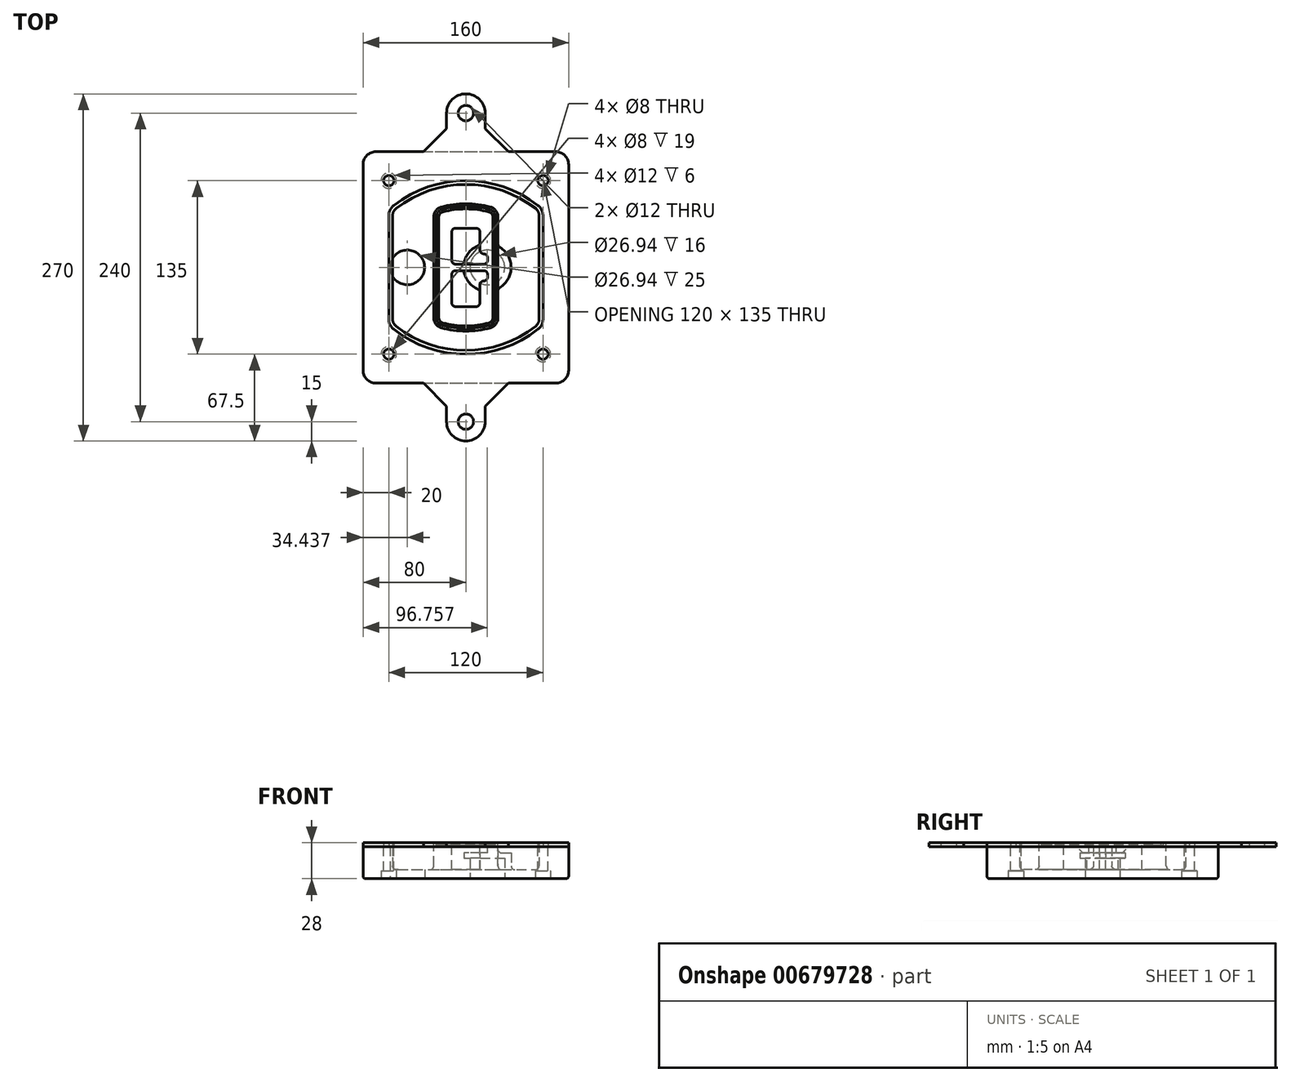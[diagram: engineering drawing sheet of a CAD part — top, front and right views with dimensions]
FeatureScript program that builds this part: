
annotation { "Feature Type Name" : "Feature", "Feature Type Description" : "" }
export const myFeature = defineFeature(function(context is Context, id is Id, definition is map)
    precondition{}
    {
        {
            var Q0;
            Q0=qCreatedBy(makeId("Top.planeOp"),FACE);
            var sketch = newSketch(context, id + "F0", { "sketchPlane" : qUnion([Q0])});
            skPoint(sketch, "E0.rect.middle", {"position": v(0, 0) * mm});
            skLineSegment(sketch, "E1.bottom", {"start": v(-70, -90) * mm, "end": v(70, -90) * mm});
            skLineSegment(sketch, "E1.top", {"start": v(-70, 90) * mm, "end": v(70, 90) * mm});
            skLineSegment(sketch, "E1.left", {"start": v(-80, -80) * mm, "end": v(-80, 80) * mm});
            skLineSegment(sketch, "E1.right", {"start": v(80, -80) * mm, "end": v(80, 80) * mm});
            skLineSegment(sketch, "E2", {"start": v(-80, 90) * mm, "end": v(80, -90) * mm, "construction": true});
            skLineSegment(sketch, "E3", {"start": v(80, 90) * mm, "end": v(-80, -90) * mm, "construction": true});
            skCircle(sketch, "E4", {"center": v(-60, 67.5) * mm, "radius": 4 * mm});
            skCircle(sketch, "E5", {"center": v(60, 67.5) * mm, "radius": 4 * mm});
            skCircle(sketch, "E6", {"center": v(60, -67.5) * mm, "radius": 4 * mm});
            skCircle(sketch, "E7", {"center": v(-60, -67.5) * mm, "radius": 4 * mm});
            skLineSegment(sketch, "E8", {"start": v(-60, 67.5) * mm, "end": v(60, 67.5) * mm, "construction": true});
            skLineSegment(sketch, "E9", {"start": v(60, 67.5) * mm, "end": v(60, -67.5) * mm, "construction": true});
            skLineSegment(sketch, "E10", {"start": v(60, -67.5) * mm, "end": v(-60, -67.5) * mm, "construction": true});
            skLineSegment(sketch, "E11", {"start": v(-60, -67.5) * mm, "end": v(-60, 67.5) * mm, "construction": true});
            skLineSegment(sketch, "E12", {"start": v(-60, 40.3) * mm, "end": v(-60, -40.3) * mm});
            skLineSegment(sketch, "E13", {"start": v(60, 40.3) * mm, "end": v(60, -40.3) * mm});
            skArc(sketch, "E14", {"start": v(56.15, 48.18) * mm, "mid": v(0, 67.5) * mm, "end": v(-56.15, 48.18) * mm});
            skArc(sketch, "E15", {"start": v(-56.15, -48.18) * mm, "mid": v(0, -67.5) * mm, "end": v(56.15, -48.18) * mm});
            skLineSegment(sketch, "E16", {"start": v(-60, 0) * mm, "end": v(60, 0) * mm, "construction": true});
            skPoint(sketch, "E17.visualSharp", {"position": v(-60, -45) * mm});
            skArc(sketch, "E17.filletArc", {"start": v(-60, -40.3) * mm, "mid": v(-58.99, -44.68) * mm, "end": v(-56.15, -48.18) * mm});
            skPoint(sketch, "E18.visualSharp", {"position": v(-60, 45) * mm});
            skArc(sketch, "E18.filletArc", {"start": v(-56.15, 48.18) * mm, "mid": v(-58.99, 44.68) * mm, "end": v(-60, 40.3) * mm});
            skPoint(sketch, "E19.visualSharp", {"position": v(60, 45) * mm});
            skArc(sketch, "E19.filletArc", {"start": v(60, 40.3) * mm, "mid": v(58.99, 44.68) * mm, "end": v(56.15, 48.18) * mm});
            skPoint(sketch, "E20.visualSharp", {"position": v(60, -45) * mm});
            skArc(sketch, "E20.filletArc", {"start": v(56.15, -48.18) * mm, "mid": v(58.99, -44.68) * mm, "end": v(60, -40.3) * mm});
            skPoint(sketch, "E21.visualSharp", {"position": v(-80, 90) * mm});
            skArc(sketch, "E21.filletArc", {"start": v(-70, 90) * mm, "mid": v(-77.07, 87.07) * mm, "end": v(-80, 80) * mm});
            skPoint(sketch, "E22.visualSharp", {"position": v(80, 90) * mm});
            skArc(sketch, "E22.filletArc", {"start": v(80, 80) * mm, "mid": v(77.07, 87.07) * mm, "end": v(70, 90) * mm});
            skPoint(sketch, "E23.visualSharp", {"position": v(80, -90) * mm});
            skArc(sketch, "E23.filletArc", {"start": v(70, -90) * mm, "mid": v(77.07, -87.07) * mm, "end": v(80, -80) * mm});
            skPoint(sketch, "E24.visualSharp", {"position": v(-80, -90) * mm});
            skArc(sketch, "E24.filletArc", {"start": v(-80, -80) * mm, "mid": v(-77.07, -87.07) * mm, "end": v(-70, -90) * mm});
            skArc(sketch, "E25.0", {"start": v(57, 40.3) * mm, "mid": v(56.3, 43.36) * mm, "end": v(54.3, 45.81) * mm});
            skLineSegment(sketch, "E25.1", {"start": v(57, 40.3) * mm, "end": v(57, -40.3) * mm});
            skArc(sketch, "E25.2", {"start": v(54.3, -45.81) * mm, "mid": v(56.3, -43.36) * mm, "end": v(57, -40.3) * mm});
            skArc(sketch, "E25.3", {"start": v(-54.3, -45.81) * mm, "mid": v(0, -64.5) * mm, "end": v(54.3, -45.81) * mm});
            skArc(sketch, "E25.4", {"start": v(-57, -40.3) * mm, "mid": v(-56.3, -43.36) * mm, "end": v(-54.3, -45.81) * mm});
            skArc(sketch, "E25.5", {"start": v(54.3, 45.81) * mm, "mid": v(0, 64.5) * mm, "end": v(-54.3, 45.81) * mm});
            skLineSegment(sketch, "E25.6", {"start": v(-57, 40.3) * mm, "end": v(-57, -40.3) * mm});
            skArc(sketch, "E25.7", {"start": v(-54.3, 45.81) * mm, "mid": v(-56.3, 43.36) * mm, "end": v(-57, 40.3) * mm});
            skArc(sketch, "E26.0", {"start": v(-58.62, 51.33) * mm, "mid": v(-62.58, 46.43) * mm, "end": v(-64, 40.3) * mm});
            skArc(sketch, "E26.1", {"start": v(58.62, 51.33) * mm, "mid": v(0, 71.5) * mm, "end": v(-58.62, 51.33) * mm});
            skArc(sketch, "E26.2", {"start": v(64, 40.3) * mm, "mid": v(62.58, 46.43) * mm, "end": v(58.62, 51.33) * mm});
            skLineSegment(sketch, "E26.3", {"start": v(64, 40.3) * mm, "end": v(64, -40.3) * mm});
            skArc(sketch, "E26.4", {"start": v(58.62, -51.33) * mm, "mid": v(62.58, -46.43) * mm, "end": v(64, -40.3) * mm});
            skLineSegment(sketch, "E26.5", {"start": v(-64, 40.3) * mm, "end": v(-64, -40.3) * mm});
            skArc(sketch, "E26.6", {"start": v(-58.62, -51.33) * mm, "mid": v(0, -71.5) * mm, "end": v(58.62, -51.33) * mm});
            skArc(sketch, "E26.7", {"start": v(-64, -40.3) * mm, "mid": v(-62.58, -46.43) * mm, "end": v(-58.62, -51.33) * mm});
            skSolve(sketch);
        }
        {
            var Q0;
            Q0=makeQuery(id+"F0.imprint","IMPRINT",FACE,{"disambiguationData":[TD([[makeQuery(id+"F0.imprint","IMPRINT",EDGE,{"derivedFrom":sQuery(id+"F0.wireOp",EDGE,"E1.bottom")}),1.0]])]});
            var Q1;
            Q1=makeQuery(id+"F0.imprint","IMPRINT",FACE,{"disambiguationData":[TD([[makeQuery(id+"F0.imprint","IMPRINT",EDGE,{"derivedFrom":sQuery(id+"F0.wireOp",EDGE,"E12")}),1.0]])]});
            var Q2;
            Q2=makeQuery(id+"F0.imprint","IMPRINT",FACE,{"disambiguationData":[TD([[makeQuery(id+"F0.imprint","IMPRINT",EDGE,{"derivedFrom":sQuery(id+"F0.wireOp",EDGE,"E25.0")}),1.0]])]});
            var Q3;
            Q3=makeQuery(id+"F0.imprint","IMPRINT",FACE,{"disambiguationData":[TD([[makeQuery(id+"F0.imprint","IMPRINT",EDGE,{"derivedFrom":sQuery(id+"F0.wireOp",EDGE,"E12")}),-1.0]])]});
            extrude(context, id + "F1", {"entities" : qUnion([Q0, Q1, Q2, Q3]), "oppositeDirection" : true, "depth" : 25 * mm});
        }
        {
            var Q0;
            Q0=makeQuery(id+"F0.imprint","IMPRINT",FACE,{"disambiguationData":[TD([[makeQuery(id+"F0.imprint","IMPRINT",EDGE,{"derivedFrom":sQuery(id+"F0.wireOp",EDGE,"E12")}),1.0]])]});
            extrude(context, id + "F2", {"entities" : qUnion([Q0]), "operationType" : NewBodyOperationType.ADD, "depth" : 3 * mm});
        }
        {
            var Q0;
            Q0=makeQuery(id+"F0.imprint","IMPRINT",FACE,{"disambiguationData":[TD([[makeQuery(id+"F0.imprint","IMPRINT",EDGE,{"derivedFrom":sQuery(id+"F0.wireOp",EDGE,"E25.0")}),1.0]])]});
            extrude(context, id + "F3", {"entities" : qUnion([Q0]), "operationType" : NewBodyOperationType.REMOVE, "oppositeDirection" : true, "depth" : 18 * mm});
        }
        {
            var Q0;
            Q0=makeQuery(id+"F2.opExtrude","CAP_FACE",FACE,{"disambiguationData":[OSD([sQuery(id+"F0.wireOp",EDGE,"E12"),sQuery(id+"F0.wireOp",EDGE,"E13"),sQuery(id+"F0.wireOp",EDGE,"E14"),sQuery(id+"F0.wireOp",EDGE,"E15"),sQuery(id+"F0.wireOp",EDGE,"E17.filletArc"),sQuery(id+"F0.wireOp",EDGE,"E18.filletArc"),sQuery(id+"F0.wireOp",EDGE,"E19.filletArc"),sQuery(id+"F0.wireOp",EDGE,"E20.filletArc"),sQuery(id+"F0.wireOp",EDGE,"E25.0"),sQuery(id+"F0.wireOp",EDGE,"E25.1"),sQuery(id+"F0.wireOp",EDGE,"E25.2"),sQuery(id+"F0.wireOp",EDGE,"E25.3"),sQuery(id+"F0.wireOp",EDGE,"E25.4"),sQuery(id+"F0.wireOp",EDGE,"E25.5"),sQuery(id+"F0.wireOp",EDGE,"E25.6"),sQuery(id+"F0.wireOp",EDGE,"E25.7")])],"isStart":false});
            var sketch = newSketch(context, id + "F4", { "sketchPlane" : qUnion([Q0])});
            skArc(sketch, "E27.0", {"start": v(-19.08, -46.97) * mm, "mid": v(0, -49.5) * mm, "end": v(19.08, -46.97) * mm});
            skArc(sketch, "E28.0", {"start": v(19.08, 46.97) * mm, "mid": v(0, 49.5) * mm, "end": v(-19.08, 46.97) * mm});
            skLineSegment(sketch, "E29", {"start": v(-25, 39.25) * mm, "end": v(-25, -39.25) * mm});
            skLineSegment(sketch, "E30", {"start": v(25, 39.25) * mm, "end": v(25, -39.25) * mm});
            skLineSegment(sketch, "E31", {"start": v(-25, 45.1) * mm, "end": v(25, 45.1) * mm, "construction": true});
            skLineSegment(sketch, "E32", {"start": v(-25, -45.1) * mm, "end": v(25, -45.1) * mm, "construction": true});
            skPoint(sketch, "E33.visualSharp", {"position": v(-25, 45.1) * mm});
            skArc(sketch, "E33.filletArc", {"start": v(-19.08, 46.97) * mm, "mid": v(-23.35, 44.11) * mm, "end": v(-25, 39.25) * mm});
            skPoint(sketch, "E34.visualSharp", {"position": v(25, 45.1) * mm});
            skArc(sketch, "E34.filletArc", {"start": v(25, 39.25) * mm, "mid": v(23.35, 44.11) * mm, "end": v(19.08, 46.97) * mm});
            skPoint(sketch, "E35.visualSharp", {"position": v(25, -45.1) * mm});
            skArc(sketch, "E35.filletArc", {"start": v(19.08, -46.97) * mm, "mid": v(23.35, -44.11) * mm, "end": v(25, -39.25) * mm});
            skPoint(sketch, "E36.visualSharp", {"position": v(-25, -45.1) * mm});
            skArc(sketch, "E36.filletArc", {"start": v(-25, -39.25) * mm, "mid": v(-23.35, -44.11) * mm, "end": v(-19.08, -46.97) * mm});
            skArc(sketch, "E37.0", {"start": v(54.3, 45.81) * mm, "mid": v(0, 64.5) * mm, "end": v(-54.3, 45.81) * mm});
            skArc(sketch, "E37.1", {"start": v(-54.3, 45.81) * mm, "mid": v(-56.3, 43.36) * mm, "end": v(-57, 40.3) * mm});
            skLineSegment(sketch, "E37.2", {"start": v(-57, 40.3) * mm, "end": v(-57, -40.3) * mm});
            skArc(sketch, "E37.3", {"start": v(-57, -40.3) * mm, "mid": v(-56.3, -43.36) * mm, "end": v(-54.3, -45.81) * mm});
            skArc(sketch, "E37.4", {"start": v(-54.3, -45.81) * mm, "mid": v(0, -64.5) * mm, "end": v(54.3, -45.81) * mm});
            skArc(sketch, "E37.5", {"start": v(54.3, -45.81) * mm, "mid": v(56.3, -43.36) * mm, "end": v(57, -40.3) * mm});
            skLineSegment(sketch, "E37.6", {"start": v(57, 40.3) * mm, "end": v(57, -40.3) * mm});
            skArc(sketch, "E37.7", {"start": v(57, 40.3) * mm, "mid": v(56.3, 43.36) * mm, "end": v(54.3, 45.81) * mm});
            skLineSegment(sketch, "E38.0", {"start": v(23, 39.25) * mm, "end": v(23, -39.25) * mm});
            skArc(sketch, "E38.1", {"start": v(18.56, -45.04) * mm, "mid": v(21.76, -42.9) * mm, "end": v(23, -39.25) * mm});
            skArc(sketch, "E38.2", {"start": v(-18.56, -45.04) * mm, "mid": v(0, -47.5) * mm, "end": v(18.56, -45.04) * mm});
            skArc(sketch, "E38.3", {"start": v(-23, -39.25) * mm, "mid": v(-21.76, -42.9) * mm, "end": v(-18.56, -45.04) * mm});
            skLineSegment(sketch, "E38.4", {"start": v(-23, 39.25) * mm, "end": v(-23, -39.25) * mm});
            skArc(sketch, "E38.5", {"start": v(23, 39.25) * mm, "mid": v(21.76, 42.9) * mm, "end": v(18.56, 45.04) * mm});
            skArc(sketch, "E38.6", {"start": v(-18.56, 45.04) * mm, "mid": v(-21.76, 42.9) * mm, "end": v(-23, 39.25) * mm});
            skArc(sketch, "E38.7", {"start": v(18.56, 45.04) * mm, "mid": v(0, 47.5) * mm, "end": v(-18.56, 45.04) * mm});
            skArc(sketch, "E39.0", {"start": v(21, 39.25) * mm, "mid": v(20.18, 41.68) * mm, "end": v(18.04, 43.1) * mm});
            skLineSegment(sketch, "E39.1", {"start": v(21, 39.25) * mm, "end": v(21, -39.25) * mm});
            skArc(sketch, "E39.2", {"start": v(18.04, -43.1) * mm, "mid": v(20.18, -41.68) * mm, "end": v(21, -39.25) * mm});
            skArc(sketch, "E39.3", {"start": v(-18.04, -43.1) * mm, "mid": v(0, -45.5) * mm, "end": v(18.04, -43.1) * mm});
            skArc(sketch, "E39.4", {"start": v(-21, -39.25) * mm, "mid": v(-20.18, -41.68) * mm, "end": v(-18.04, -43.1) * mm});
            skArc(sketch, "E39.5", {"start": v(18.04, 43.1) * mm, "mid": v(0, 45.5) * mm, "end": v(-18.04, 43.1) * mm});
            skLineSegment(sketch, "E39.6", {"start": v(-21, 39.25) * mm, "end": v(-21, -39.25) * mm});
            skArc(sketch, "E39.7", {"start": v(-18.04, 43.1) * mm, "mid": v(-20.18, 41.68) * mm, "end": v(-21, 39.25) * mm});
            skLineSegment(sketch, "E40", {"start": v(-25, 0) * mm, "end": v(25, 0) * mm, "construction": true});
            skLineSegment(sketch, "E41", {"start": v(-11, 5.5) * mm, "end": v(-11, 27.5) * mm});
            skLineSegment(sketch, "E42", {"start": v(-8, 30.5) * mm, "end": v(8, 30.5) * mm});
            skLineSegment(sketch, "E43", {"start": v(11, 27.5) * mm, "end": v(11, 13.5) * mm});
            skLineSegment(sketch, "E44", {"start": v(14, 10.5) * mm, "end": v(14, 10.5) * mm});
            skLineSegment(sketch, "E45", {"start": v(17, 7.5) * mm, "end": v(17, 5.5) * mm});
            skLineSegment(sketch, "E46", {"start": v(14, 2.5) * mm, "end": v(-8, 2.5) * mm});
            skPoint(sketch, "E47.visualSharp", {"position": v(-11, 30.5) * mm});
            skArc(sketch, "E47.filletArc", {"start": v(-8, 30.5) * mm, "mid": v(-10.12, 29.62) * mm, "end": v(-11, 27.5) * mm});
            skPoint(sketch, "E48.visualSharp", {"position": v(11, 30.5) * mm});
            skArc(sketch, "E48.filletArc", {"start": v(11, 27.5) * mm, "mid": v(10.12, 29.62) * mm, "end": v(8, 30.5) * mm});
            skPoint(sketch, "E49.visualSharp", {"position": v(11, 10.5) * mm});
            skArc(sketch, "E49.filletArc", {"start": v(11, 13.5) * mm, "mid": v(11.88, 11.38) * mm, "end": v(14, 10.5) * mm});
            skPoint(sketch, "E50.visualSharp", {"position": v(17, 10.5) * mm});
            skArc(sketch, "E50.filletArc", {"start": v(17, 7.5) * mm, "mid": v(16.12, 9.62) * mm, "end": v(14, 10.5) * mm});
            skPoint(sketch, "E51.visualSharp", {"position": v(17, 2.5) * mm});
            skArc(sketch, "E51.filletArc", {"start": v(14, 2.5) * mm, "mid": v(16.12, 3.38) * mm, "end": v(17, 5.5) * mm});
            skPoint(sketch, "E52.visualSharp", {"position": v(-11, 2.5) * mm});
            skArc(sketch, "E52.filletArc", {"start": v(-11, 5.5) * mm, "mid": v(-10.12, 3.38) * mm, "end": v(-8, 2.5) * mm});
            skLineSegment(sketch, "E53.0.MirrorCS", {"start": v(14, -2.5) * mm, "end": v(-8, -2.5) * mm});
            skArc(sketch, "E54.0.MirrorCS", {"start": v(-11, -5.5) * mm, "mid": v(-10.12, -3.38) * mm, "end": v(-8, -2.5) * mm});
            skLineSegment(sketch, "E55.0.MirrorCS", {"start": v(-11, -5.5) * mm, "end": v(-11, -27.5) * mm});
            skArc(sketch, "E56.0.MirrorCS", {"start": v(-8, -30.5) * mm, "mid": v(-10.12, -29.62) * mm, "end": v(-11, -27.5) * mm});
            skLineSegment(sketch, "E57.0.MirrorCS", {"start": v(-8, -30.5) * mm, "end": v(8, -30.5) * mm});
            skArc(sketch, "E58.0.MirrorCS", {"start": v(11, -27.5) * mm, "mid": v(10.12, -29.62) * mm, "end": v(8, -30.5) * mm});
            skLineSegment(sketch, "E59.0.MirrorCS", {"start": v(11, -27.5) * mm, "end": v(11, -13.5) * mm});
            skArc(sketch, "E60.0.MirrorCS", {"start": v(11, -13.5) * mm, "mid": v(11.88, -11.38) * mm, "end": v(14, -10.5) * mm});
            skArc(sketch, "E61.0.MirrorCS", {"start": v(17, -7.5) * mm, "mid": v(16.12, -9.62) * mm, "end": v(14, -10.5) * mm});
            skLineSegment(sketch, "E62.0.MirrorCS", {"start": v(17, -7.5) * mm, "end": v(17, -5.5) * mm});
            skArc(sketch, "E63.0.MirrorCS", {"start": v(14, -2.5) * mm, "mid": v(16.12, -3.38) * mm, "end": v(17, -5.5) * mm});
            skSolve(sketch);
        }
        {
            var Q0;
            Q0=makeQuery(id+"F4.imprint","IMPRINT",FACE,{"disambiguationData":[TD([[makeQuery(id+"F4.imprint","IMPRINT",EDGE,{"derivedFrom":sQuery(id+"F4.wireOp",EDGE,"E27.0")}),1.0]])]});
            var Q1;
            Q1=makeQuery(id+"F4.imprint","IMPRINT",FACE,{"disambiguationData":[TD([[makeQuery(id+"F4.imprint","IMPRINT",EDGE,{"derivedFrom":sQuery(id+"F4.wireOp",EDGE,"E38.0")}),-1.0]])]});
            var Q2;
            Q2=makeQuery(id+"F4.imprint","IMPRINT",FACE,{"disambiguationData":[TD([[makeQuery(id+"F4.imprint","IMPRINT",EDGE,{"derivedFrom":sQuery(id+"F4.wireOp",EDGE,"E39.0")}),1.0]])]});
            extrude(context, id + "F5", {"entities" : qUnion([Q0, Q1, Q2]), "operationType" : NewBodyOperationType.ADD, "endBound" : BoundingType.UP_TO_NEXT, "oppositeDirection" : true, "depth" : 25 * mm});
        }
        {
            var Q0;
            Q0=makeQuery(id+"F4.imprint","IMPRINT",FACE,{"disambiguationData":[TD([[makeQuery(id+"F4.imprint","IMPRINT",EDGE,{"derivedFrom":sQuery(id+"F4.wireOp",EDGE,"E38.0")}),-1.0]])]});
            extrude(context, id + "F6", {"entities" : qUnion([Q0]), "operationType" : NewBodyOperationType.REMOVE, "oppositeDirection" : true, "depth" : 2 * mm});
        }
        {
            var Q0;
            Q0=makeQuery(id+"F1.opExtrude","CAP_FACE",FACE,{"disambiguationData":[OSD([sQuery(id+"F0.wireOp",EDGE,"E1.bottom"),sQuery(id+"F0.wireOp",EDGE,"E1.top"),sQuery(id+"F0.wireOp",EDGE,"E1.left"),sQuery(id+"F0.wireOp",EDGE,"E1.right"),sQuery(id+"F0.wireOp",EDGE,"E4"),sQuery(id+"F0.wireOp",EDGE,"E5"),sQuery(id+"F0.wireOp",EDGE,"E6"),sQuery(id+"F0.wireOp",EDGE,"E7"),sQuery(id+"F0.wireOp",EDGE,"E21.filletArc"),sQuery(id+"F0.wireOp",EDGE,"E22.filletArc"),sQuery(id+"F0.wireOp",EDGE,"E23.filletArc"),sQuery(id+"F0.wireOp",EDGE,"E24.filletArc")])],"isStart":false});
            var sketch = newSketch(context, id + "F7", { "sketchPlane" : qUnion([Q0])});
            skCircle(sketch, "E64", {"center": v(16.76, 0) * mm, "radius": 13.47 * mm});
            skCircle(sketch, "E65", {"center": v(-45.56, 0) * mm, "radius": 13.47 * mm});
            skLineSegment(sketch, "E66", {"start": v(80, 0) * mm, "end": v(-80, 0) * mm});
            skCircle(sketch, "E67", {"center": v(16.76, 0) * mm, "radius": 18.47 * mm});
            skCircle(sketch, "E68", {"center": v(60, -67.5) * mm, "radius": 6 * mm});
            skCircle(sketch, "E69", {"center": v(-60, -67.5) * mm, "radius": 6 * mm});
            skCircle(sketch, "E70", {"center": v(-60, 67.5) * mm, "radius": 6 * mm});
            skCircle(sketch, "E71", {"center": v(60, 67.5) * mm, "radius": 6 * mm});
            skSolve(sketch);
        }
        {
            var Q0;
            {var subQ1=sQuery(id+"F7.wireOp",EDGE,"E66");var subQ4=sQuery(id+"F7.wireOp",EDGE,"E64");var subQ6=makeQuery(id+"F7.imprint","INTERSECT",VERTEX,{"disambiguationData":[OD(0.0)],"derivedFrom":[subQ4,subQ1]});Q0=makeQuery(id+"F7.imprint","IMPRINT",FACE,{"disambiguationData":[TD([[makeQuery(id+"F7.imprint","IMPRINT",EDGE,{"disambiguationData":[TD([[subQ6,-1.0]])],"derivedFrom":subQ4}),-1.0]])]});}
            var Q1;
            {var subQ0=sQuery(id+"F7.wireOp",EDGE,"E66");var subQ1=sQuery(id+"F7.wireOp",EDGE,"E64");var subQ3=makeQuery(id+"F7.imprint","INTERSECT",VERTEX,{"disambiguationData":[OD(0.0)],"derivedFrom":[subQ1,subQ0]});Q1=makeQuery(id+"F7.imprint","IMPRINT",FACE,{"disambiguationData":[TD([[makeQuery(id+"F7.imprint","IMPRINT",EDGE,{"disambiguationData":[TD([[subQ3,-1.0]])],"derivedFrom":subQ1}),1.0]])]});}
            var Q2;
            {var subQ0=sQuery(id+"F7.wireOp",EDGE,"E66");var subQ1=sQuery(id+"F7.wireOp",EDGE,"E64");var subQ3=makeQuery(id+"F7.imprint","INTERSECT",VERTEX,{"disambiguationData":[OD(0.0)],"derivedFrom":[subQ1,subQ0]});Q2=makeQuery(id+"F7.imprint","IMPRINT",FACE,{"disambiguationData":[TD([[makeQuery(id+"F7.imprint","IMPRINT",EDGE,{"disambiguationData":[TD([[subQ3,1.0]])],"derivedFrom":subQ1}),1.0]])]});}
            var Q3;
            {var subQ1=sQuery(id+"F7.wireOp",EDGE,"E66");var subQ4=sQuery(id+"F7.wireOp",EDGE,"E64");var subQ6=makeQuery(id+"F7.imprint","INTERSECT",VERTEX,{"disambiguationData":[OD(0.0)],"derivedFrom":[subQ4,subQ1]});Q3=makeQuery(id+"F7.imprint","IMPRINT",FACE,{"disambiguationData":[TD([[makeQuery(id+"F7.imprint","IMPRINT",EDGE,{"disambiguationData":[TD([[subQ6,1.0]])],"derivedFrom":subQ4}),-1.0]])]});}
            extrude(context, id + "F8", {"entities" : qUnion([Q0, Q1, Q2, Q3]), "operationType" : NewBodyOperationType.ADD, "oppositeDirection" : true, "depth" : 20 * mm});
        }
        {
            var Q0;
            {var subQ0=sQuery(id+"F7.wireOp",EDGE,"E66");var subQ1=sQuery(id+"F7.wireOp",EDGE,"E64");var subQ3=makeQuery(id+"F7.imprint","INTERSECT",VERTEX,{"disambiguationData":[OD(0.0)],"derivedFrom":[subQ1,subQ0]});Q0=makeQuery(id+"F7.imprint","IMPRINT",FACE,{"disambiguationData":[TD([[makeQuery(id+"F7.imprint","IMPRINT",EDGE,{"disambiguationData":[TD([[subQ3,-1.0]])],"derivedFrom":subQ1}),1.0]])]});}
            var Q1;
            {var subQ0=sQuery(id+"F7.wireOp",EDGE,"E66");var subQ1=sQuery(id+"F7.wireOp",EDGE,"E64");var subQ3=makeQuery(id+"F7.imprint","INTERSECT",VERTEX,{"disambiguationData":[OD(0.0)],"derivedFrom":[subQ1,subQ0]});Q1=makeQuery(id+"F7.imprint","IMPRINT",FACE,{"disambiguationData":[TD([[makeQuery(id+"F7.imprint","IMPRINT",EDGE,{"disambiguationData":[TD([[subQ3,1.0]])],"derivedFrom":subQ1}),1.0]])]});}
            extrude(context, id + "F9", {"entities" : qUnion([Q0, Q1]), "operationType" : NewBodyOperationType.REMOVE, "oppositeDirection" : true, "depth" : 16 * mm});
        }
        {
            var Q0;
            {var subQ0=sQuery(id+"F7.wireOp",EDGE,"E66");var subQ1=sQuery(id+"F7.wireOp",EDGE,"E65");var subQ3=makeQuery(id+"F7.imprint","INTERSECT",VERTEX,{"disambiguationData":[OD(0.0)],"derivedFrom":[subQ1,subQ0]});Q0=makeQuery(id+"F7.imprint","IMPRINT",FACE,{"disambiguationData":[TD([[makeQuery(id+"F7.imprint","IMPRINT",EDGE,{"disambiguationData":[TD([[subQ3,-1.0]])],"derivedFrom":subQ1}),1.0]])]});}
            var Q1;
            {var subQ0=sQuery(id+"F7.wireOp",EDGE,"E66");var subQ1=sQuery(id+"F7.wireOp",EDGE,"E65");var subQ3=makeQuery(id+"F7.imprint","INTERSECT",VERTEX,{"disambiguationData":[OD(0.0)],"derivedFrom":[subQ1,subQ0]});Q1=makeQuery(id+"F7.imprint","IMPRINT",FACE,{"disambiguationData":[TD([[makeQuery(id+"F7.imprint","IMPRINT",EDGE,{"disambiguationData":[TD([[subQ3,1.0]])],"derivedFrom":subQ1}),1.0]])]});}
            extrude(context, id + "F10", {"entities" : qUnion([Q0, Q1]), "operationType" : NewBodyOperationType.REMOVE, "oppositeDirection" : true, "depth" : 25 * mm});
        }
        {
            var Q0;
            Q0=makeQuery(id+"F7.imprint","IMPRINT",FACE,{"disambiguationData":[TD([[makeQuery(id+"F7.imprint","IMPRINT",EDGE,{"derivedFrom":sQuery(id+"F7.wireOp",EDGE,"E68")}),1.0]])]});
            var Q1;
            Q1=makeQuery(id+"F7.imprint","IMPRINT",FACE,{"disambiguationData":[TD([[makeQuery(id+"F7.imprint","IMPRINT",EDGE,{"derivedFrom":makeQuery(id+"F1.opExtrude","CAP_EDGE",EDGE,{"disambiguationData":[OSD([sQuery(id+"F0.wireOp",EDGE,"E5")])],"isStart":false})}),-1.0]])]});
            var Q2;
            Q2=makeQuery(id+"F7.imprint","IMPRINT",FACE,{"disambiguationData":[TD([[makeQuery(id+"F7.imprint","IMPRINT",EDGE,{"derivedFrom":sQuery(id+"F7.wireOp",EDGE,"E69")}),1.0]])]});
            var Q3;
            Q3=makeQuery(id+"F7.imprint","IMPRINT",FACE,{"disambiguationData":[TD([[makeQuery(id+"F7.imprint","IMPRINT",EDGE,{"derivedFrom":makeQuery(id+"F1.opExtrude","CAP_EDGE",EDGE,{"disambiguationData":[OSD([sQuery(id+"F0.wireOp",EDGE,"E4")])],"isStart":false})}),-1.0]])]});
            var Q4;
            Q4=makeQuery(id+"F7.imprint","IMPRINT",FACE,{"disambiguationData":[TD([[makeQuery(id+"F7.imprint","IMPRINT",EDGE,{"derivedFrom":sQuery(id+"F7.wireOp",EDGE,"E70")}),1.0]])]});
            var Q5;
            Q5=makeQuery(id+"F7.imprint","IMPRINT",FACE,{"disambiguationData":[TD([[makeQuery(id+"F7.imprint","IMPRINT",EDGE,{"derivedFrom":makeQuery(id+"F1.opExtrude","CAP_EDGE",EDGE,{"disambiguationData":[OSD([sQuery(id+"F0.wireOp",EDGE,"E7")])],"isStart":false})}),-1.0]])]});
            var Q6;
            Q6=makeQuery(id+"F7.imprint","IMPRINT",FACE,{"disambiguationData":[TD([[makeQuery(id+"F7.imprint","IMPRINT",EDGE,{"derivedFrom":sQuery(id+"F7.wireOp",EDGE,"E71")}),1.0]])]});
            var Q7;
            Q7=makeQuery(id+"F7.imprint","IMPRINT",FACE,{"disambiguationData":[TD([[makeQuery(id+"F7.imprint","IMPRINT",EDGE,{"derivedFrom":makeQuery(id+"F1.opExtrude","CAP_EDGE",EDGE,{"disambiguationData":[OSD([sQuery(id+"F0.wireOp",EDGE,"E6")])],"isStart":false})}),-1.0]])]});
            extrude(context, id + "F11", {"entities" : qUnion([Q0, Q1, Q2, Q3, Q4, Q5, Q6, Q7]), "operationType" : NewBodyOperationType.REMOVE, "oppositeDirection" : true, "depth" : 6 * mm});
        }
        {
            var Q0;
            Q0=makeQuery(id+"F9.boolean.opBoolean","COPY",FACE,{"derivedFrom":makeQuery(id+"F9.opExtrude","CAP_FACE",FACE,{"disambiguationData":[OSD([sQuery(id+"F7.wireOp",EDGE,"E64")])],"isStart":false})});
            var sketch = newSketch(context, id + "F12", { "sketchPlane" : qUnion([Q0])});
            skArc(sketch, "E72.0", {"start": v(11, 17.55) * mm, "mid": v(2.57, 11.82) * mm, "end": v(-1.54, 2.5) * mm});
            skArc(sketch, "E72.1", {"start": v(-1.54, -2.5) * mm, "mid": v(2.57, -11.82) * mm, "end": v(11, -17.55) * mm});
            skLineSegment(sketch, "E73", {"start": v(-1.54, -2.5) * mm, "end": v(14, -2.5) * mm});
            skLineSegment(sketch, "E74.0", {"start": v(14, 2.5) * mm, "end": v(-1.54, 2.5) * mm});
            skArc(sketch, "E74.1", {"start": v(14, 2.5) * mm, "mid": v(16.12, 3.38) * mm, "end": v(17, 5.5) * mm});
            skLineSegment(sketch, "E74.2", {"start": v(17, 7.5) * mm, "end": v(17, 5.5) * mm});
            skArc(sketch, "E74.3", {"start": v(17, 7.5) * mm, "mid": v(16.12, 9.62) * mm, "end": v(14, 10.5) * mm});
            skArc(sketch, "E74.4", {"start": v(11, 13.5) * mm, "mid": v(11.88, 11.38) * mm, "end": v(14, 10.5) * mm});
            skLineSegment(sketch, "E74.5", {"start": v(11, 17.55) * mm, "end": v(11, 13.5) * mm});
            skLineSegment(sketch, "E74.7", {"start": v(14, -2.5) * mm, "end": v(-1.54, -2.5) * mm});
            skArc(sketch, "E74.8", {"start": v(14, -2.5) * mm, "mid": v(16.12, -3.38) * mm, "end": v(17, -5.5) * mm});
            skLineSegment(sketch, "E74.9", {"start": v(17, -7.5) * mm, "end": v(17, -5.5) * mm});
            skArc(sketch, "E74.10", {"start": v(17, -7.5) * mm, "mid": v(16.12, -9.62) * mm, "end": v(14, -10.5) * mm});
            skArc(sketch, "E74.11", {"start": v(11, -13.5) * mm, "mid": v(11.88, -11.38) * mm, "end": v(14, -10.5) * mm});
            skLineSegment(sketch, "E74.12", {"start": v(11, -17.55) * mm, "end": v(11, -13.5) * mm});
            skPoint(sketch, "E75.orphan", {"position": v(11, -27.5) * mm});
            skPoint(sketch, "E76.orphan", {"position": v(-8, -2.5) * mm});
            skPoint(sketch, "E77.orphan", {"position": v(-8, 2.5) * mm});
            skPoint(sketch, "E78.orphan", {"position": v(11, 27.5) * mm});
            skSolve(sketch);
        }
        {
            var Q0;
            {var subQ7=sQuery(id+"F12.wireOp",EDGE,"E72.0");var subQ14=sQuery(id+"F12.wireOp",EDGE,"E72.1");var subQ16=sQuery(id+"F12.wireOp",EDGE,"E74.1");var subQ18=sQuery(id+"F12.wireOp",EDGE,"E74.8");Q0=qUnion([makeQuery(id+"F12.imprint","IMPRINT",FACE,{"disambiguationData":[TD([[makeQuery(id+"F12.imprint","IMPRINT",EDGE,{"derivedFrom":subQ7}),1.0]])]}),makeQuery(id+"F12.imprint","IMPRINT",FACE,{"disambiguationData":[TD([[makeQuery(id+"F12.imprint","IMPRINT",EDGE,{"derivedFrom":subQ14}),1.0]])]}),makeQuery(id+"F12.imprint","IMPRINT",FACE,{"disambiguationData":[TD([[makeQuery(id+"F12.imprint","IMPRINT",EDGE,{"derivedFrom":subQ16}),1.0]])]}),makeQuery(id+"F12.imprint","IMPRINT",FACE,{"disambiguationData":[TD([[makeQuery(id+"F12.imprint","IMPRINT",EDGE,{"derivedFrom":subQ18}),-1.0]])]})]);}
            var Q1;
            Q1=makeQuery(id+"F5.boolean.opBoolean","SPLIT",FACE,{"disambiguationData":[TD([makeQuery(id+"F5.opExtrude","SWEPT_FACE",FACE,{"disambiguationData":[OSD([sQuery(id+"F4.wireOp",EDGE,"E41")])]})])],"derivedFrom":makeQuery(id+"F3.boolean.opBoolean","COPY",FACE,{"derivedFrom":makeQuery(id+"F3.opExtrude","CAP_FACE",FACE,{"disambiguationData":[OSD([sQuery(id+"F0.wireOp",EDGE,"E25.0"),sQuery(id+"F0.wireOp",EDGE,"E25.1"),sQuery(id+"F0.wireOp",EDGE,"E25.2"),sQuery(id+"F0.wireOp",EDGE,"E25.3"),sQuery(id+"F0.wireOp",EDGE,"E25.4"),sQuery(id+"F0.wireOp",EDGE,"E25.5"),sQuery(id+"F0.wireOp",EDGE,"E25.6"),sQuery(id+"F0.wireOp",EDGE,"E25.7")])],"isStart":false})})});
            extrude(context, id + "F13", {"entities" : qUnion([Q0]), "operationType" : NewBodyOperationType.REMOVE, "endBound" : BoundingType.UP_TO_SURFACE, "endBoundEntityFace" : qUnion([Q1]), "depth" : 25 * mm});
        }
        {
            var Q0;
            Q0=makeQuery(id+"F3.boolean.opBoolean","COPY",EDGE,{"derivedFrom":makeQuery(id+"F3.opExtrude","CAP_EDGE",EDGE,{"disambiguationData":[OSD([sQuery(id+"F0.wireOp",EDGE,"E25.6")])],"isStart":false})});
            var Q1;
            Q1=makeQuery(id+"F8.boolean.opBoolean","INTERSECT",EDGE,{"derivedFrom":[makeQuery(id+"F5.opExtrude","SWEPT_FACE",FACE,{"disambiguationData":[OSD([sQuery(id+"F4.wireOp",EDGE,"E30")])]}),makeQuery(id+"F8.opExtrude","CAP_FACE",FACE,{"disambiguationData":[OSD([sQuery(id+"F7.wireOp",EDGE,"E67")])],"isStart":false})]});
            var Q2;
            Q2=makeQuery(id+"F8.boolean.opBoolean","INTERSECT",EDGE,{"disambiguationData":[OD(1.0)],"derivedFrom":[makeQuery(id+"F5.opExtrude","SWEPT_FACE",FACE,{"disambiguationData":[OSD([sQuery(id+"F4.wireOp",EDGE,"E30")])]}),makeQuery(id+"F8.opExtrude","SWEPT_FACE",FACE,{"disambiguationData":[OSD([sQuery(id+"F7.wireOp",EDGE,"E67")])]})]});
            var Q3;
            {var subQ0=sQuery(id+"F4.wireOp",EDGE,"E30");Q3=makeQuery(id+"F8.boolean.opBoolean","SPLIT",EDGE,{"disambiguationData":[TD([makeQuery(id+"F5.opExtrude","SWEPT_FACE",FACE,{"disambiguationData":[OSD([sQuery(id+"F4.wireOp",EDGE,"E35.filletArc")])]})])],"derivedFrom":makeQuery(id+"F5.opExtrude","CAP_EDGE",EDGE,{"disambiguationData":[OSD([subQ0])],"isStart":false})});}
            var Q4;
            {var subQ0=sQuery(id+"F0.wireOp",EDGE,"E25.7");var subQ1=sQuery(id+"F0.wireOp",EDGE,"E25.1");var subQ2=sQuery(id+"F0.wireOp",EDGE,"E25.6");var subQ3=sQuery(id+"F0.wireOp",EDGE,"E25.5");var subQ4=sQuery(id+"F0.wireOp",EDGE,"E25.4");var subQ5=sQuery(id+"F0.wireOp",EDGE,"E25.0");var subQ6=sQuery(id+"F0.wireOp",EDGE,"E25.2");var subQ7=sQuery(id+"F0.wireOp",EDGE,"E25.3");Q4=makeQuery(id+"F8.boolean.opBoolean","INTERSECT",EDGE,{"derivedFrom":[makeQuery(id+"F5.boolean.opBoolean","SPLIT",FACE,{"disambiguationData":[TD([makeQuery(id+"F2.opExtrude","SWEPT_FACE",FACE,{"disambiguationData":[OSD([subQ5])]})])],"derivedFrom":makeQuery(id+"F3.boolean.opBoolean","COPY",FACE,{"derivedFrom":makeQuery(id+"F3.opExtrude","CAP_FACE",FACE,{"disambiguationData":[OSD([subQ5,subQ1,subQ6,subQ7,subQ4,subQ3,subQ2,subQ0])],"isStart":false})})}),makeQuery(id+"F8.opExtrude","SWEPT_FACE",FACE,{"disambiguationData":[OSD([sQuery(id+"F7.wireOp",EDGE,"E67")])]})]});}
            var Q5;
            Q5=makeQuery(id+"F8.boolean.opBoolean","INTERSECT",EDGE,{"disambiguationData":[OD(0.0)],"derivedFrom":[makeQuery(id+"F5.opExtrude","SWEPT_FACE",FACE,{"disambiguationData":[OSD([sQuery(id+"F4.wireOp",EDGE,"E30")])]}),makeQuery(id+"F8.opExtrude","SWEPT_FACE",FACE,{"disambiguationData":[OSD([sQuery(id+"F7.wireOp",EDGE,"E67")])]})]});
            fillet(context, id + "F14", {"entities" : qUnion([Q0, Q1, Q2, Q3, Q4, Q5]), "radius" : 3 * mm, "tangentPropagation" : true, "allowEdgeOverflow" : false});
        }
        {
            var Q0;
            Q0=makeQuery(id+"F1.opExtrude","CAP_EDGE",EDGE,{"disambiguationData":[OSD([sQuery(id+"F0.wireOp",EDGE,"E1.bottom")])],"isStart":false});
            fillet(context, id + "F15", {"entities" : qUnion([Q0]), "radius" : 2 * mm, "tangentPropagation" : true, "allowEdgeOverflow" : false});
        }
        {
            var Q0;
            {var subQ0=sQuery(id+"F0.wireOp",EDGE,"E21.filletArc");var subQ1=sQuery(id+"F0.wireOp",EDGE,"E7");var subQ2=sQuery(id+"F0.wireOp",EDGE,"E6");var subQ3=sQuery(id+"F0.wireOp",EDGE,"E5");var subQ4=sQuery(id+"F0.wireOp",EDGE,"E4");var subQ5=sQuery(id+"F0.wireOp",EDGE,"E22.filletArc");var subQ6=sQuery(id+"F0.wireOp",EDGE,"E1.bottom");var subQ7=sQuery(id+"F0.wireOp",EDGE,"E1.right");var subQ8=sQuery(id+"F0.wireOp",EDGE,"E1.top");var subQ9=sQuery(id+"F0.wireOp",EDGE,"E1.left");var subQ10=sQuery(id+"F0.wireOp",EDGE,"E23.filletArc");var subQ11=sQuery(id+"F0.wireOp",EDGE,"E24.filletArc");Q0=makeQuery(id+"F2.boolean.opBoolean","SPLIT",FACE,{"disambiguationData":[TD([makeQuery(id+"F1.opExtrude","SWEPT_FACE",FACE,{"disambiguationData":[OSD([subQ6])]})])],"derivedFrom":makeQuery(id+"F1.opExtrude","CAP_FACE",FACE,{"disambiguationData":[OSD([subQ6,subQ8,subQ9,subQ7,subQ4,subQ3,subQ2,subQ1,subQ0,subQ5,subQ10,subQ11])],"isStart":true})});}
            var sketch = newSketch(context, id + "F16", { "sketchPlane" : qUnion([Q0])});
            skLineSegment(sketch, "E79.0", {"start": v(-80, -80) * mm, "end": v(-80, 80) * mm});
            skArc(sketch, "E79.1", {"start": v(-80, -80) * mm, "mid": v(-77.07, -87.07) * mm, "end": v(-70, -90) * mm});
            skLineSegment(sketch, "E79.2", {"start": v(-70, -90) * mm, "end": v(70, -90) * mm});
            skArc(sketch, "E79.3", {"start": v(70, -90) * mm, "mid": v(77.07, -87.07) * mm, "end": v(80, -80) * mm});
            skLineSegment(sketch, "E79.4", {"start": v(80, -80) * mm, "end": v(80, 80) * mm});
            skArc(sketch, "E79.5", {"start": v(80, 80) * mm, "mid": v(77.07, 87.07) * mm, "end": v(70, 90) * mm});
            skLineSegment(sketch, "E79.6", {"start": v(-70, 90) * mm, "end": v(70, 90) * mm});
            skArc(sketch, "E79.7", {"start": v(-70, 90) * mm, "mid": v(-77.07, 87.07) * mm, "end": v(-80, 80) * mm});
            skLineSegment(sketch, "E79.8", {"start": v(-60, 40.3) * mm, "end": v(-60, -40.3) * mm});
            skArc(sketch, "E79.9", {"start": v(-56.15, -48.18) * mm, "mid": v(0, -67.5) * mm, "end": v(56.15, -48.18) * mm});
            skLineSegment(sketch, "E79.10", {"start": v(60, 40.3) * mm, "end": v(60, -40.3) * mm});
            skArc(sketch, "E79.11", {"start": v(56.15, 48.18) * mm, "mid": v(0, 67.5) * mm, "end": v(-56.15, 48.18) * mm});
            skArc(sketch, "E79.12", {"start": v(60, 40.3) * mm, "mid": v(58.99, 44.68) * mm, "end": v(56.15, 48.18) * mm});
            skArc(sketch, "E79.13", {"start": v(56.15, -48.18) * mm, "mid": v(58.99, -44.68) * mm, "end": v(60, -40.3) * mm});
            skArc(sketch, "E79.14", {"start": v(-56.15, 48.18) * mm, "mid": v(-58.99, 44.68) * mm, "end": v(-60, 40.3) * mm});
            skArc(sketch, "E79.15", {"start": v(-60, -40.3) * mm, "mid": v(-58.99, -44.68) * mm, "end": v(-56.15, -48.18) * mm});
            skCircle(sketch, "E79.16", {"center": v(-60, -67.5) * mm, "radius": 4 * mm});
            skCircle(sketch, "E79.17", {"center": v(60, -67.5) * mm, "radius": 4 * mm});
            skCircle(sketch, "E79.18", {"center": v(60, 67.5) * mm, "radius": 4 * mm});
            skCircle(sketch, "E79.19", {"center": v(-60, 67.5) * mm, "radius": 4 * mm});
            skLineSegment(sketch, "E80", {"start": v(0, 90) * mm, "end": v(0, 120) * mm, "construction": true});
            skCircle(sketch, "E81", {"center": v(0, 120) * mm, "radius": 6 * mm});
            skArc(sketch, "E82", {"start": v(15, 120) * mm, "mid": v(0, 135) * mm, "end": v(-15, 120) * mm});
            skLineSegment(sketch, "E83", {"start": v(-15, 120) * mm, "end": v(-15, 108) * mm});
            skLineSegment(sketch, "E84", {"start": v(-15, 108) * mm, "end": v(-33, 90) * mm});
            skLineSegment(sketch, "E85", {"start": v(15, 120) * mm, "end": v(15, 108) * mm});
            skLineSegment(sketch, "E86", {"start": v(15, 108) * mm, "end": v(33, 90) * mm});
            skLineSegment(sketch, "E87", {"start": v(93.35, 0) * mm, "end": v(-87.03, 0) * mm, "construction": true});
            skLineSegment(sketch, "E88.MirrorCS", {"start": v(-15, -108) * mm, "end": v(-33, -90) * mm});
            skLineSegment(sketch, "E89.MirrorCS", {"start": v(15, -120) * mm, "end": v(15, -108) * mm});
            skLineSegment(sketch, "E90.MirrorCS", {"start": v(0, -90) * mm, "end": v(0, -120) * mm, "construction": true});
            skLineSegment(sketch, "E91.MirrorCS", {"start": v(-15, -120) * mm, "end": v(-15, -108) * mm});
            skCircle(sketch, "E92.MirrorC", {"center": v(0, -120) * mm, "radius": 6 * mm});
            skLineSegment(sketch, "E93.MirrorCS", {"start": v(15, -108) * mm, "end": v(33, -90) * mm});
            skArc(sketch, "E94.MirrorCS", {"start": v(15, -120) * mm, "mid": v(0, -135) * mm, "end": v(-15, -120) * mm});
            skSolve(sketch);
        }
        {
            var Q0;
            Q0=makeQuery(id+"F16.imprint","IMPRINT",FACE,{"disambiguationData":[TD([[makeQuery(id+"F16.imprint","IMPRINT",EDGE,{"derivedFrom":sQuery(id+"F16.wireOp",EDGE,"E79.0")}),-1.0]])]});
            var Q1;
            Q1=makeQuery(id+"F16.imprint","IMPRINT",FACE,{"disambiguationData":[TD([[makeQuery(id+"F16.imprint","IMPRINT",EDGE,{"derivedFrom":sQuery(id+"F16.wireOp",EDGE,"E81")}),-1.0]])]});
            var Q2;
            {var subQ0=sQuery(id+"F16.wireOp",EDGE,"E88.MirrorCS");Q2=makeQuery(id+"F16.imprint","IMPRINT",FACE,{"disambiguationData":[TD([[makeQuery(id+"F16.imprint","IMPRINT",EDGE,{"derivedFrom":subQ0}),-1.0]])]});}
            var Q3;
            Q3=makeQuery(id+"F2.opExtrude","CAP_FACE",FACE,{"disambiguationData":[OSD([sQuery(id+"F0.wireOp",EDGE,"E12"),sQuery(id+"F0.wireOp",EDGE,"E13"),sQuery(id+"F0.wireOp",EDGE,"E14"),sQuery(id+"F0.wireOp",EDGE,"E15"),sQuery(id+"F0.wireOp",EDGE,"E17.filletArc"),sQuery(id+"F0.wireOp",EDGE,"E18.filletArc"),sQuery(id+"F0.wireOp",EDGE,"E19.filletArc"),sQuery(id+"F0.wireOp",EDGE,"E20.filletArc"),sQuery(id+"F0.wireOp",EDGE,"E25.0"),sQuery(id+"F0.wireOp",EDGE,"E25.1"),sQuery(id+"F0.wireOp",EDGE,"E25.2"),sQuery(id+"F0.wireOp",EDGE,"E25.3"),sQuery(id+"F0.wireOp",EDGE,"E25.4"),sQuery(id+"F0.wireOp",EDGE,"E25.5"),sQuery(id+"F0.wireOp",EDGE,"E25.6"),sQuery(id+"F0.wireOp",EDGE,"E25.7")])],"isStart":false});
            extrude(context, id + "F17", {"entities" : qUnion([Q0, Q1, Q2]), "endBound" : BoundingType.UP_TO_SURFACE, "depth" : 25 * mm, "endBoundEntityFace" : qUnion([Q3]), "offsetDistance" : 25 * mm});
        }
    });
